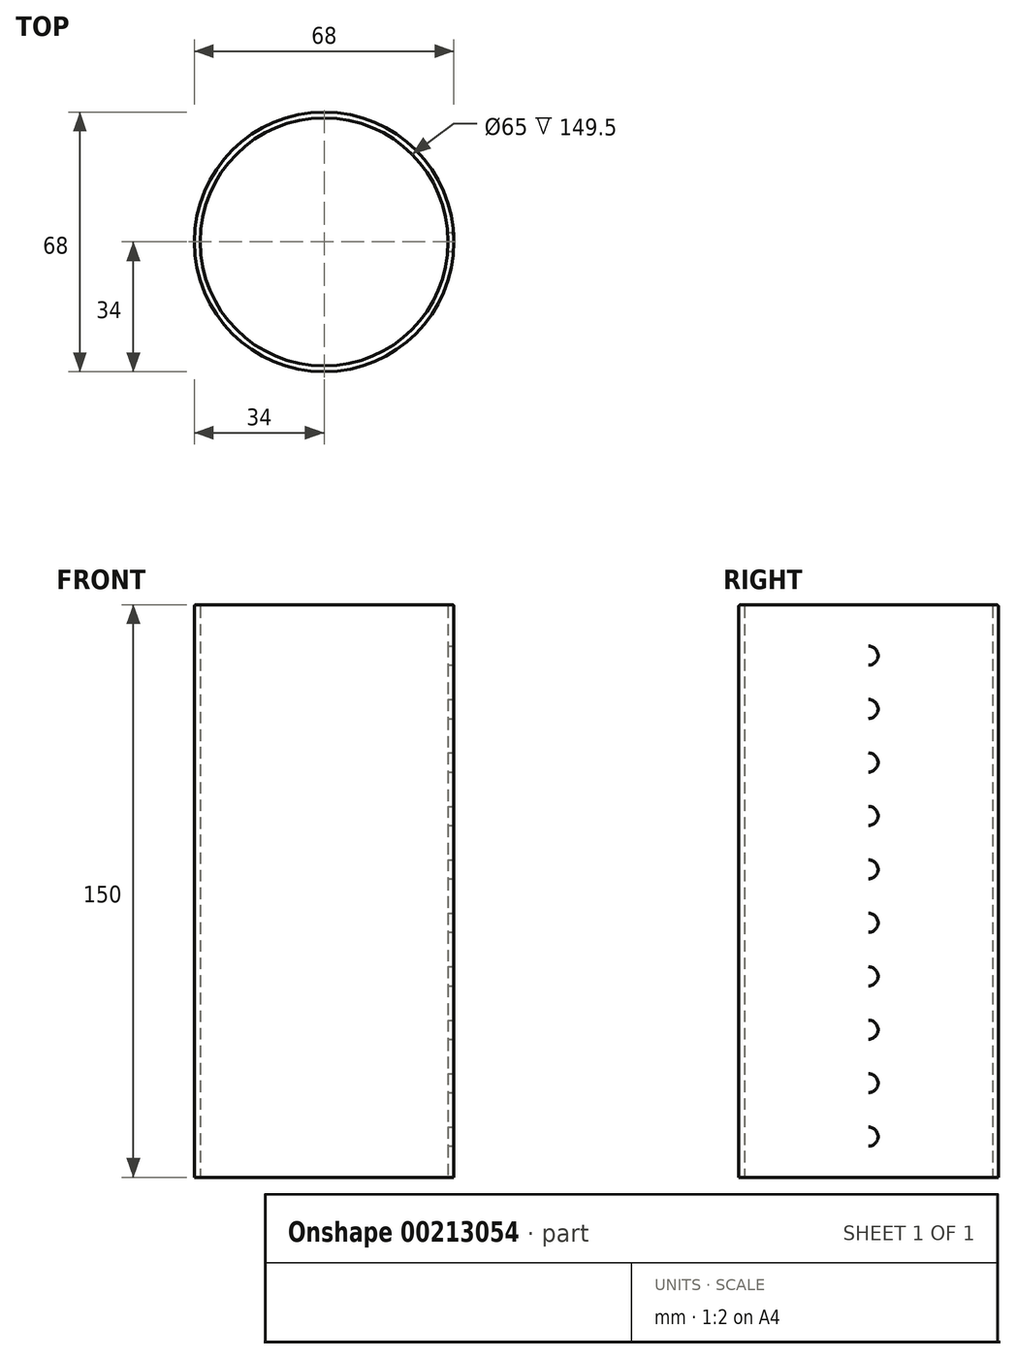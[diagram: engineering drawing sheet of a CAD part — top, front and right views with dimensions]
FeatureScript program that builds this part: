
annotation { "Feature Type Name" : "Feature", "Feature Type Description" : "" }
export const myFeature = defineFeature(function(context is Context, id is Id, definition is map)
    precondition{}
    {
        {
            var Q0;
            Q0=qCreatedBy(makeId("Top.planeOp"),FACE);
            var sketch = newSketch(context, id + "F0", { "sketchPlane" : qUnion([Q0])});
            skCircle(sketch, "E0", {"center": v(0, 0) * mm, "radius": 34 * mm});
            skCircle(sketch, "E1", {"center": v(0, 0) * mm, "radius": 32.5 * mm});
            skSolve(sketch);
        }
        {
            var Q0;
            Q0=makeQuery(id+"F0.imprint","IMPRINT",FACE,{"disambiguationData":[TD([[makeQuery(id+"F0.imprint","IMPRINT",EDGE,{"derivedFrom":sQuery(id+"F0.wireOp",EDGE,"E0")}),1.0]])]});
            extrude(context, id + "F1", {"entities" : qUnion([Q0]), "depth" : 150 * mm});
        }
        {
            var Q0;
            Q0=qCreatedBy(makeId("Right.planeOp"),FACE);
            cPlane(context, id + "F2", {"entities" : qUnion([Q0]), "cplaneType" : CPlaneType.OFFSET, "offset" : 50 * mm, "width" : 150 * mm, "height" : 150 * mm});
        }
        {
            var Q0;
            Q0=qCreatedBy(id+"F2.planeOp",FACE);
            var sketch = newSketch(context, id + "F3", { "sketchPlane" : qUnion([Q0])});
            skCircle(sketch, "E2", {"center": v(0, 10.66) * mm, "radius": 2.5 * mm});
            skCircle(sketch, "E3.0.1.0", {"center": v(0, 24.66) * mm, "radius": 2.5 * mm});
            skCircle(sketch, "E3.0.2.0", {"center": v(0, 38.66) * mm, "radius": 2.5 * mm});
            skCircle(sketch, "E3.0.3.0", {"center": v(0, 52.66) * mm, "radius": 2.5 * mm});
            skCircle(sketch, "E3.0.4.0", {"center": v(0, 66.66) * mm, "radius": 2.5 * mm});
            skCircle(sketch, "E3.0.5.0", {"center": v(0, 80.66) * mm, "radius": 2.5 * mm});
            skCircle(sketch, "E3.0.6.0", {"center": v(0, 94.66) * mm, "radius": 2.5 * mm});
            skCircle(sketch, "E3.0.7.0", {"center": v(0, 108.66) * mm, "radius": 2.5 * mm});
            skCircle(sketch, "E3.0.8.0", {"center": v(0, 122.66) * mm, "radius": 2.5 * mm});
            skCircle(sketch, "E3.0.9.0", {"center": v(0, 136.66) * mm, "radius": 2.5 * mm});
            skLineSegment(sketch, "E3.direction1", {"start": v(0, 10.66) * mm, "end": v(25, 10.66) * mm, "construction": true});
            skLineSegment(sketch, "E3.direction2", {"start": v(0, 10.66) * mm, "end": v(0, 24.66) * mm, "construction": true});
            skSolve(sketch);
        }
        {
            var Q0;
            Q0=makeQuery(id+"F3.imprint","IMPRINT",FACE,{"disambiguationData":[TD([[makeQuery(id+"F3.imprint","IMPRINT",EDGE,{"derivedFrom":sQuery(id+"F3.wireOp",EDGE,"E3.0.9.0")}),1.0]])]});
            var Q1;
            Q1=makeQuery(id+"F3.imprint","IMPRINT",FACE,{"disambiguationData":[TD([[makeQuery(id+"F3.imprint","IMPRINT",EDGE,{"derivedFrom":sQuery(id+"F3.wireOp",EDGE,"E3.0.8.0")}),1.0]])]});
            var Q2;
            Q2=makeQuery(id+"F3.imprint","IMPRINT",FACE,{"disambiguationData":[TD([[makeQuery(id+"F3.imprint","IMPRINT",EDGE,{"derivedFrom":sQuery(id+"F3.wireOp",EDGE,"E3.0.7.0")}),1.0]])]});
            var Q3;
            Q3=makeQuery(id+"F3.imprint","IMPRINT",FACE,{"disambiguationData":[TD([[makeQuery(id+"F3.imprint","IMPRINT",EDGE,{"derivedFrom":sQuery(id+"F3.wireOp",EDGE,"E3.0.6.0")}),1.0]])]});
            var Q4;
            Q4=makeQuery(id+"F3.imprint","IMPRINT",FACE,{"disambiguationData":[TD([[makeQuery(id+"F3.imprint","IMPRINT",EDGE,{"derivedFrom":sQuery(id+"F3.wireOp",EDGE,"E3.0.5.0")}),1.0]])]});
            var Q5;
            Q5=makeQuery(id+"F3.imprint","IMPRINT",FACE,{"disambiguationData":[TD([[makeQuery(id+"F3.imprint","IMPRINT",EDGE,{"derivedFrom":sQuery(id+"F3.wireOp",EDGE,"E3.0.4.0")}),1.0]])]});
            var Q6;
            Q6=makeQuery(id+"F3.imprint","IMPRINT",FACE,{"disambiguationData":[TD([[makeQuery(id+"F3.imprint","IMPRINT",EDGE,{"derivedFrom":sQuery(id+"F3.wireOp",EDGE,"E3.0.3.0")}),1.0]])]});
            var Q7;
            Q7=makeQuery(id+"F3.imprint","IMPRINT",FACE,{"disambiguationData":[TD([[makeQuery(id+"F3.imprint","IMPRINT",EDGE,{"derivedFrom":sQuery(id+"F3.wireOp",EDGE,"E3.0.2.0")}),1.0]])]});
            var Q8;
            Q8=makeQuery(id+"F3.imprint","IMPRINT",FACE,{"disambiguationData":[TD([[makeQuery(id+"F3.imprint","IMPRINT",EDGE,{"derivedFrom":sQuery(id+"F3.wireOp",EDGE,"E3.0.1.0")}),1.0]])]});
            var Q9;
            Q9=makeQuery(id+"F3.imprint","IMPRINT",FACE,{"disambiguationData":[TD([[makeQuery(id+"F3.imprint","IMPRINT",EDGE,{"derivedFrom":sQuery(id+"F3.wireOp",EDGE,"E2")}),1.0]])]});
            extrude(context, id + "F4", {"entities" : qUnion([Q0, Q1, Q2, Q3, Q4, Q5, Q6, Q7, Q8, Q9]), "operationType" : NewBodyOperationType.REMOVE, "oppositeDirection" : true, "depth" : 25 * mm});
        }
        {
            var Q0;
            Q0=makeQuery(id+"F1.opExtrude","CAP_EDGE",EDGE,{"disambiguationData":[OSD([sQuery(id+"F0.wireOp",EDGE,"E0")])],"isStart":false});
            var Q1;
            Q1=makeQuery(id+"F1.opExtrude","CAP_EDGE",EDGE,{"disambiguationData":[OSD([sQuery(id+"F0.wireOp",EDGE,"E1")])],"isStart":false});
            fillet(context, id + "F5", {"entities" : qUnion([Q0, Q1]), "radius" : 0.5 * mm, "tangentPropagation" : true, "allowEdgeOverflow" : false});
        }
    });
